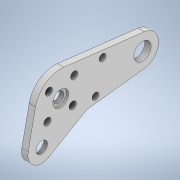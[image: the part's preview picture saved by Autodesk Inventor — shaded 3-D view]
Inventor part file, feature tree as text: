
AUTODESK INVENTOR PART (.ipt)
format: ipt  version: 2020 (Build 240168000, 168)  size: 268,800 bytes
history: native  units: mm
features: extrude x7, sketch x4, projected_geometry x3
ambient origin geometry x8: Origin, YZ Plane, XZ Plane, XY Plane, X Axis, Y Axis, Z Axis, Center Point
bodies: Body1 (feature_tree)
feature tree (14):
  extrude  "Выдавливание4"  Depth=18.6mm
  extrude  "Выдавливание5"  Depth=12.2mm
  extrude  "Выдавливание6"  Depth=9.7mm
  extrude  "Выдавливание7"  Depth=7.1mm
  sketch  "Эскиз7"
  extrude  "Выдавливание8"  Depth=38.82013mm
  extrude  "Выдавливание9"  Depth=38.8mm
  extrude  "Выдавливание10"  Depth=38.8mm
  sketch  "Эскиз4"
  projected_geometry  "Спроецированная петля3"
  sketch  "Эскиз5"
  sketch  "Эскиз6"
  projected_geometry  "Спроецированная петля4"
  projected_geometry  "Спроецированная петля5"
